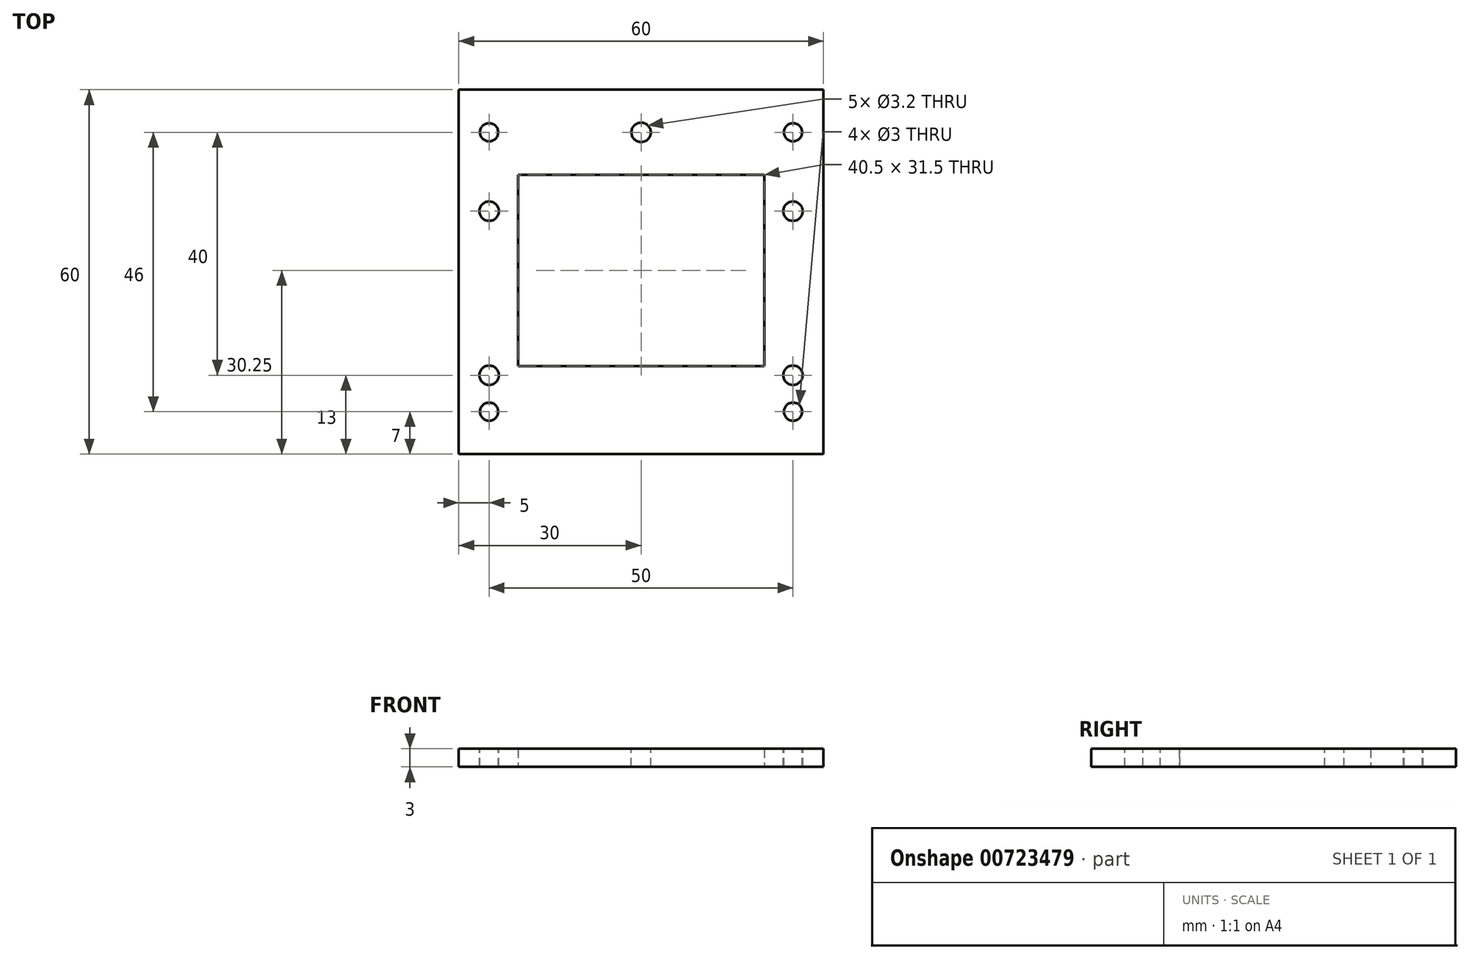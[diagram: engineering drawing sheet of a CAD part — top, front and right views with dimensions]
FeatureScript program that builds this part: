
annotation { "Feature Type Name" : "Feature", "Feature Type Description" : "" }
export const myFeature = defineFeature(function(context is Context, id is Id, definition is map)
    precondition{}
    {
        {
            var Q0;
            Q0=qCreatedBy(makeId("Top.planeOp"),FACE);
            var sketch = newSketch(context, id + "F0", { "sketchPlane" : qUnion([Q0])});
            skLineSegment(sketch, "E0.bottom", {"start": v(30, 30) * mm, "end": v(-30, 30) * mm});
            skLineSegment(sketch, "E0.top", {"start": v(30, -30) * mm, "end": v(-30, -30) * mm});
            skLineSegment(sketch, "E0.left", {"start": v(30, 30) * mm, "end": v(30, -30) * mm});
            skLineSegment(sketch, "E0.right", {"start": v(-30, 30) * mm, "end": v(-30, -30) * mm});
            skPoint(sketch, "E0.middle", {"position": v(0, 0) * mm});
            skLineSegment(sketch, "E1.bottom", {"start": v(20.25, 15.5) * mm, "end": v(-20.25, 15.5) * mm});
            skLineSegment(sketch, "E1.top", {"start": v(20.25, -15.5) * mm, "end": v(-20.25, -15.5) * mm});
            skLineSegment(sketch, "E1.left", {"start": v(20.25, 15.5) * mm, "end": v(20.25, -15.5) * mm});
            skLineSegment(sketch, "E1.right", {"start": v(-20.25, 15.5) * mm, "end": v(-20.25, -15.5) * mm});
            skSolve(sketch);
        }
        {
            var Q0;
            Q0=makeQuery(id+"F0.imprint","IMPRINT",FACE,{"disambiguationData":[TD([[makeQuery(id+"F0.imprint","IMPRINT",EDGE,{"derivedFrom":sQuery(id+"F0.wireOp",EDGE,"E0.bottom")}),1.0]])]});
            extrude(context, id + "F1", {"entities" : qUnion([Q0]), "depth" : 3 * mm, "offsetDistance" : 25 * mm});
        }
        {
            var Q0;
            Q0=makeQuery(id+"F1.opExtrude","CAP_FACE",FACE,{"disambiguationData":[OSD([sQuery(id+"F0.wireOp",EDGE,"E0.bottom"),sQuery(id+"F0.wireOp",EDGE,"E0.top"),sQuery(id+"F0.wireOp",EDGE,"E0.left"),sQuery(id+"F0.wireOp",EDGE,"E0.right"),sQuery(id+"F0.wireOp",EDGE,"E1.bottom"),sQuery(id+"F0.wireOp",EDGE,"E1.top"),sQuery(id+"F0.wireOp",EDGE,"E1.left"),sQuery(id+"F0.wireOp",EDGE,"E1.right")])],"isStart":false});
            var sketch = newSketch(context, id + "F2", { "sketchPlane" : qUnion([Q0])});
            skCircle(sketch, "E2", {"center": v(-25, -23) * mm, "radius": 1.5 * mm});
            skCircle(sketch, "E3", {"center": v(-25, 23) * mm, "radius": 1.5 * mm});
            skCircle(sketch, "E4", {"center": v(25, 23) * mm, "radius": 1.5 * mm});
            skCircle(sketch, "E5", {"center": v(25, -23) * mm, "radius": 1.5 * mm});
            skSolve(sketch);
        }
        {
            var Q0;
            Q0 = qSketchRegion(id + "F2", true);
            extrude(context, id + "F3", {"entities" : qUnion([Q0]), "operationType" : NewBodyOperationType.REMOVE, "endBound" : BoundingType.THROUGH_ALL, "oppositeDirection" : true, "depth" : 25 * mm, "offsetDistance" : 25 * mm});
        }
        {
            var Q0;
            Q0=makeQuery(id+"F1.opExtrude","SWEPT_FACE",FACE,{"disambiguationData":[OSD([sQuery(id+"F0.wireOp",EDGE,"E1.bottom")])]});
            var sketch = newSketch(context, id + "F4", { "sketchPlane" : qUnion([Q0])});
            skLineSegment(sketch, "E6.bottom", {"start": v(-20.25, 3) * mm, "end": v(20.25, 3) * mm});
            skLineSegment(sketch, "E6.top", {"start": v(-20.25, 0) * mm, "end": v(20.25, 0) * mm});
            skLineSegment(sketch, "E6.left", {"start": v(-20.25, 3) * mm, "end": v(-20.25, 0) * mm});
            skLineSegment(sketch, "E6.right", {"start": v(20.25, 3) * mm, "end": v(20.25, 0) * mm});
            skSolve(sketch);
        }
        {
            var Q0;
            Q0 = qSketchRegion(id + "F4", true);
            extrude(context, id + "F5", {"entities" : qUnion([Q0]), "operationType" : NewBodyOperationType.REMOVE, "oppositeDirection" : true, "depth" : 0.5 * mm, "offsetDistance" : 25 * mm});
        }
        {
            var Q0;
            Q0=makeQuery(id+"F1.opExtrude","CAP_FACE",FACE,{"disambiguationData":[OSD([sQuery(id+"F0.wireOp",EDGE,"E0.bottom"),sQuery(id+"F0.wireOp",EDGE,"E0.top"),sQuery(id+"F0.wireOp",EDGE,"E0.left"),sQuery(id+"F0.wireOp",EDGE,"E0.right"),sQuery(id+"F0.wireOp",EDGE,"E1.bottom"),sQuery(id+"F0.wireOp",EDGE,"E1.top"),sQuery(id+"F0.wireOp",EDGE,"E1.left"),sQuery(id+"F0.wireOp",EDGE,"E1.right")])],"isStart":false});
            var sketch = newSketch(context, id + "F6", { "sketchPlane" : qUnion([Q0])});
            skCircle(sketch, "E7", {"center": v(-25, 10) * mm, "radius": 1.6 * mm});
            skCircle(sketch, "E8", {"center": v(-25, -17) * mm, "radius": 1.6 * mm});
            skCircle(sketch, "E9", {"center": v(25, 10) * mm, "radius": 1.6 * mm});
            skCircle(sketch, "E10", {"center": v(25, -17) * mm, "radius": 1.6 * mm});
            skCircle(sketch, "E11", {"center": v(0, 23) * mm, "radius": 1.6 * mm});
            skSolve(sketch);
        }
        {
            var Q0;
            Q0 = qSketchRegion(id + "F6", true);
            extrude(context, id + "F7", {"entities" : qUnion([Q0]), "operationType" : NewBodyOperationType.REMOVE, "endBound" : BoundingType.THROUGH_ALL, "oppositeDirection" : true, "depth" : 25 * mm, "offsetDistance" : 25 * mm});
        }
    });
